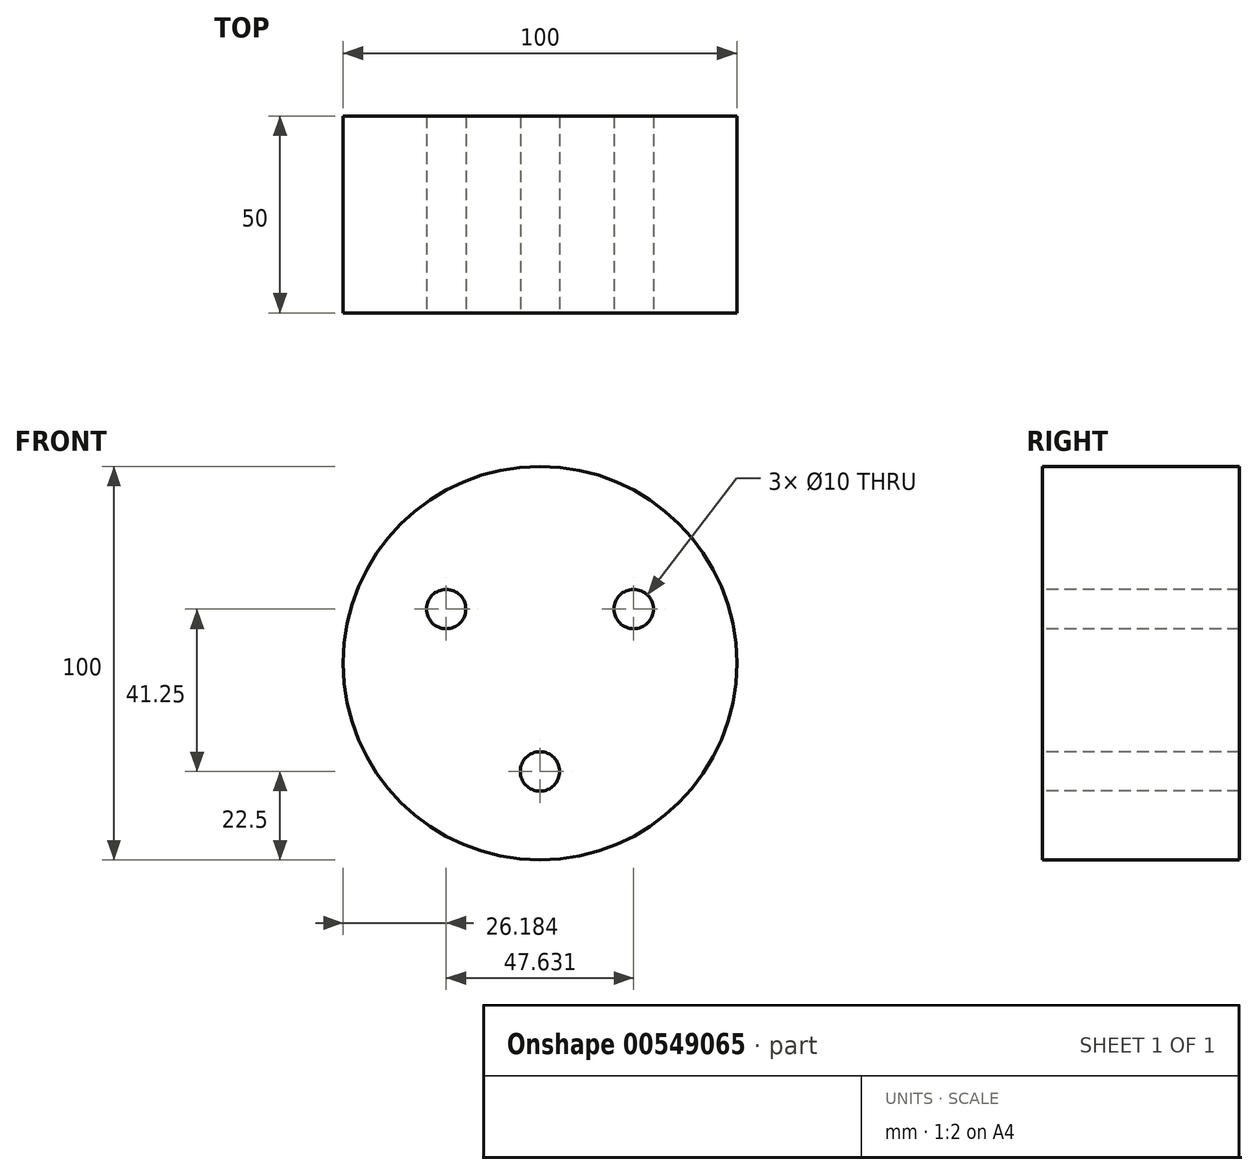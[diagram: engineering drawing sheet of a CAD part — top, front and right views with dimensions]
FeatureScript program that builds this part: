
annotation { "Feature Type Name" : "Feature", "Feature Type Description" : "" }
export const myFeature = defineFeature(function(context is Context, id is Id, definition is map)
    precondition{}
    {
        {
            var Q0;
            Q0=qCreatedBy(makeId("Front.planeOp"),FACE);
            var sketch = newSketch(context, id + "F0", { "sketchPlane" : qUnion([Q0])});
            skCircle(sketch, "E0", {"center": v(0, 0) * mm, "radius": 50 * mm});
            skSolve(sketch);
        }
        {
            var Q0;
            Q0=qSketchRegion(id+"F0",true);
            extrude(context, id + "F1", {"entities" : qUnion([Q0]), "endBound" : BoundingType.SYMMETRIC, "depth" : 50 * mm, "offsetDistance" : 25 * mm});
        }
        {
            var Q0;
            Q0=makeQuery(id+"F1.opExtrude","CAP_FACE",FACE,{"disambiguationData":[OSD([sQuery(id+"F0.wireOp",EDGE,"E0")])],"isStart":false});
            var sketch = newSketch(context, id + "F2", { "sketchPlane" : qUnion([Q0])});
            skCircle(sketch, "E1", {"center": v(-23.82, 13.75) * mm, "radius": 5 * mm});
            skCircle(sketch, "E2", {"center": v(0, -27.5) * mm, "radius": 5 * mm});
            skCircle(sketch, "E3", {"center": v(23.82, 13.75) * mm, "radius": 5 * mm});
            skCircle(sketch, "E4", {"center": v(0, 0) * mm, "radius": 27.5 * mm, "construction": true});
            skLineSegment(sketch, "E5", {"start": v(0, 0) * mm, "end": v(-54.43, 31.42) * mm});
            skLineSegment(sketch, "E6", {"start": v(0, 0) * mm, "end": v(52.16, 30.12) * mm});
            skSolve(sketch);
        }
        {
            var Q0;
            Q0=qSketchRegion(id+"F2",true);
            extrude(context, id + "F3", {"entities" : qUnion([Q0]), "operationType" : NewBodyOperationType.REMOVE, "oppositeDirection" : true, "depth" : 74 * mm, "offsetDistance" : 25 * mm});
        }
    });
